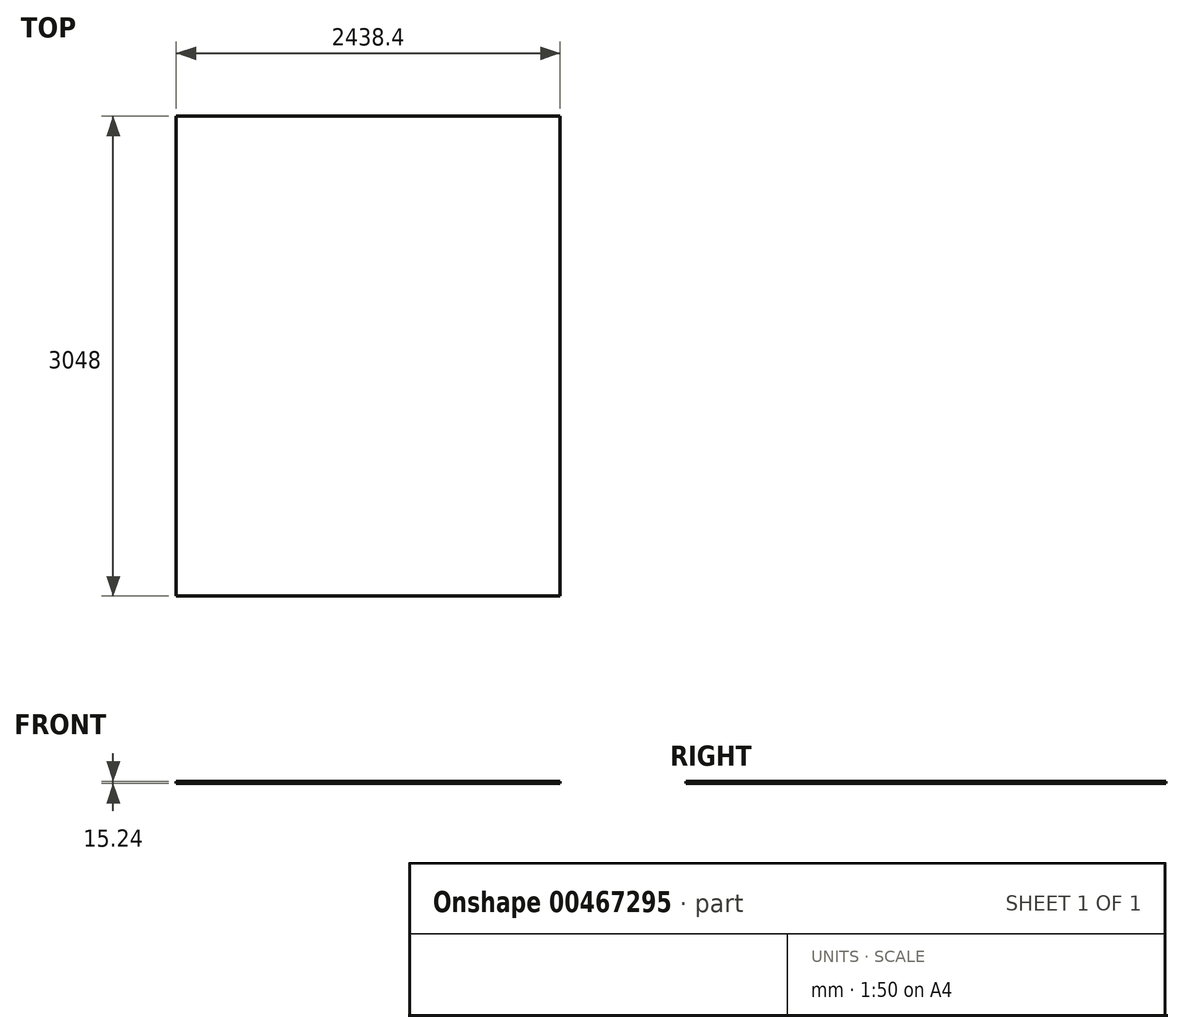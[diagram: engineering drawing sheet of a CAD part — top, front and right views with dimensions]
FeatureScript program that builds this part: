
annotation { "Feature Type Name" : "Feature", "Feature Type Description" : "" }
export const myFeature = defineFeature(function(context is Context, id is Id, definition is map)
    precondition{}
    {
        {
            var Q0;
            Q0=qCreatedBy(makeId("Top.planeOp"),FACE);
            var sketch = newSketch(context, id + "F0", { "sketchPlane" : qUnion([Q0])});
            skLineSegment(sketch, "E0.bottom", {"start": v(-1219.2, 1524) * mm, "end": v(1219.2, 1524) * mm});
            skLineSegment(sketch, "E0.top", {"start": v(-1219.2, -1524) * mm, "end": v(1219.2, -1524) * mm});
            skLineSegment(sketch, "E0.left", {"start": v(-1219.2, 1524) * mm, "end": v(-1219.2, -1524) * mm});
            skLineSegment(sketch, "E0.right", {"start": v(1219.2, 1524) * mm, "end": v(1219.2, -1524) * mm});
            skPoint(sketch, "E0.middle", {"position": v(0, 0) * mm});
            skSolve(sketch);
        }
        {
            var Q0;
            Q0 = qSketchRegion(id + "F0", true);
            extrude(context, id + "F1", {"entities" : qUnion([Q0]), "oppositeDirection" : true, "depth" : 15.24 * mm});
        }
    });
